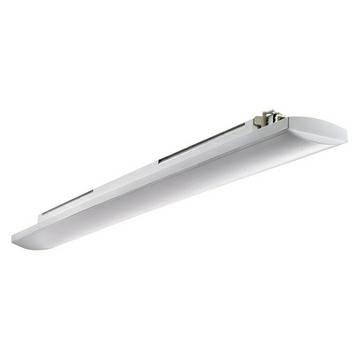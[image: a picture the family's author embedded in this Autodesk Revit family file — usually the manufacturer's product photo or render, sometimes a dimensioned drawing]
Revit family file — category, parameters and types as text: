
# Revit family: Lighting-Industriale-GEWISS-SMART[3]PLUS-PLAFONIERA-LED_OPALE_800mm
name_source: partatom
category: Apparecchi per illuminazione
units: mm (PartAtom-declared; Revit-internal decimal feet)

## family parameters
Condiviso = No
Host = Superficie
Punto di calcolo locali = No
Quota connettore circolare = Usa diametro
Sorgente d'illuminazione = Sì
Taglio con vuoti quando caricato = No
Tipo di parte = Normale

## types (1)
- Lighting-Industriale-GEWISS-SMART[3]PLUS-PLAFONIERA-LED_OPALE_800mm
    Angolo inclinazione = -90.00°
    Applicazione = Interno
    Carico apparente = 27 VA
    Catalogo = LIGHTING
    Catalogo Serie = SMART[3] PLUS
    Classe di efficienza LED integrati = A ÷ A++
    Classe isolamento = II
    Codice Electrocod = 2434
    Commenti sul wattaggio = 27W
    Descrizione = SMART3 PLUS 800 T.W.DALI HE OPAL 9 57
    Emetti da lunghezza linea = 700 mm  [stored 2.29659 ft]
    File diagramma fotometrico = GWS3123AP957.IES
    Filtro dei colori = 16777215
    Ganci = GEWISS  - ALLUMINIO
    Garanzia = 5 anni
    Glow Wire Test = 850°C
    Grado di protezione = IP66/IP69
    IDF = 8047064a-7320-478f-ab33-f9612cf1fa24
    IDT = 19b5daac-664e-44b9-8ac3-cb33faf625fb
    Immagine tipo = GWS3118P.jpg
    Lampada = LED
    Lampada: = LED
    Lumen output (lm) = 2700
    Lunghezza = 800 mm
    Lunghezza Lampada = 800 mm  [stored 2.62467 ft]
    Modello = GWS3123AP957
    Potenza di sistema = 26 W
    Produttore = GEWISS S.p.A.
    Prospetto di default = 1219 mm
    Resistenza agli urti = IK08
    SEO = Plafoniera
    Scheda Tecnica = https://www.gewiss.com
    Schermo = Opale
    Schermo. = Gewiss - Led Acceso
    Stampa 1_100 = Sì
    Stampa 1_200 = No
    Struttura = GEWISS - SMART 3 - GRIGIO
    Temperatura di colore = 5700 K (CRI > 90)
    Temperatura di colore: = 5700 K (CRI > 90)
    Temperatura di funzionamento = -25 +50 °C
    Temperatura di utilizzo = -25 +50 °C
    Tensione = 220-240 V
    Tipologia = DALI
    Tipologia sorgente luminosa = LED - Non sostituibile
    URL = https://www.gewiss.com
    Variazione temperatura colore lampada con luminosità attenuata = <Nessuno>
    Versione file RFA = 20.0

note: [stored X ft] marks values corroborated as IEEE doubles in the binary element streams (Revit-internal decimal feet)
